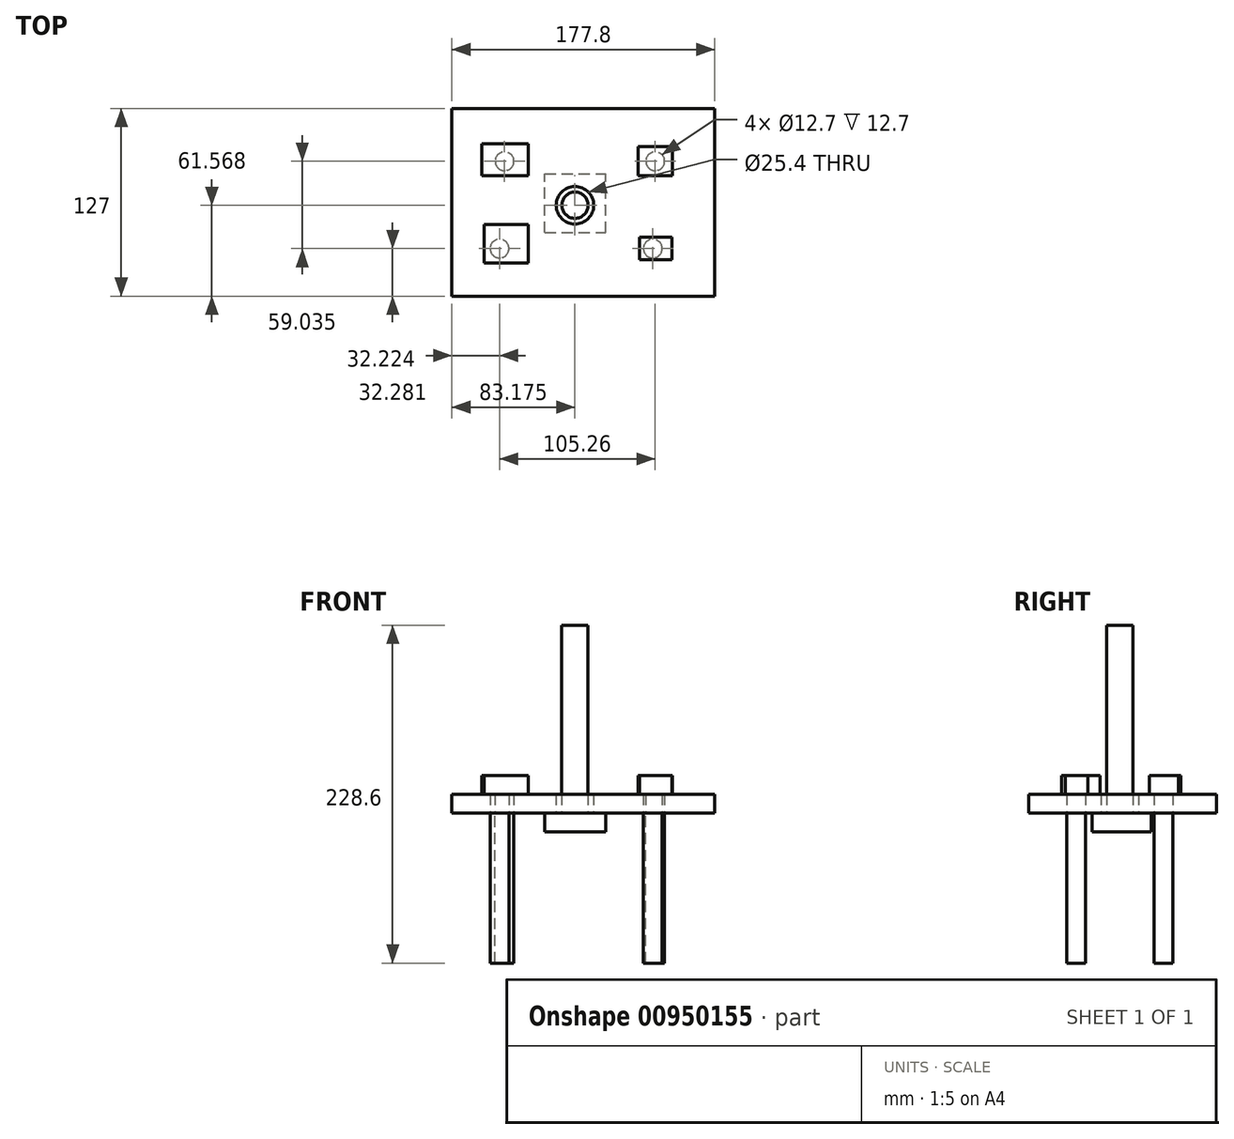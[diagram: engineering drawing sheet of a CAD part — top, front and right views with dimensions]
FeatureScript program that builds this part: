
annotation { "Feature Type Name" : "Feature", "Feature Type Description" : "" }
export const myFeature = defineFeature(function(context is Context, id is Id, definition is map)
    precondition{}
    {
        {
            var Q0;
            Q0=qCreatedBy(makeId("Top.planeOp"),FACE);
            var sketch = newSketch(context, id + "F0", { "sketchPlane" : qUnion([Q0])});
            skLineSegment(sketch, "E0.bottom", {"start": v(0, 0) * mm, "end": v(177.8, 0) * mm});
            skLineSegment(sketch, "E0.top", {"start": v(0, -127) * mm, "end": v(177.8, -127) * mm});
            skLineSegment(sketch, "E0.left", {"start": v(0, 0) * mm, "end": v(0, -127) * mm});
            skLineSegment(sketch, "E0.right", {"start": v(177.8, 0) * mm, "end": v(177.8, -127) * mm});
            skSolve(sketch);
        }
        {
            var Q0;
            Q0 = qSketchRegion(id + "F0", true);
            extrude(context, id + "F1", {"entities" : qUnion([Q0]), "depth" : 12.7 * mm, "offsetDistance" : 25.4 * mm});
        }
        {
            var Q0;
            Q0=makeQuery(id+"F1.opExtrude","CAP_FACE",FACE,{"disambiguationData":[OSD([sQuery(id+"F0.wireOp",EDGE,"E0.bottom"),sQuery(id+"F0.wireOp",EDGE,"E0.top"),sQuery(id+"F0.wireOp",EDGE,"E0.left"),sQuery(id+"F0.wireOp",EDGE,"E0.right")])],"isStart":true});
            var sketch = newSketch(context, id + "F2", { "sketchPlane" : qUnion([Q0])});
            skCircle(sketch, "E1", {"center": v(83.17, 65.43) * mm, "radius": 12.7 * mm});
            skCircle(sketch, "E2", {"center": v(135.81, 94.72) * mm, "radius": 6.35 * mm});
            skCircle(sketch, "E3", {"center": v(137.48, 35.68) * mm, "radius": 6.35 * mm});
            skCircle(sketch, "E4", {"center": v(35.57, 35.68) * mm, "radius": 6.35 * mm});
            skCircle(sketch, "E5", {"center": v(32.22, 94.72) * mm, "radius": 6.35 * mm});
            skSolve(sketch);
        }
        {
            var Q0;
            Q0 = qSketchRegion(id + "F2", true);
            extrude(context, id + "F3", {"entities" : qUnion([Q0]), "operationType" : NewBodyOperationType.REMOVE, "oppositeDirection" : true, "depth" : 25.4 * mm, "offsetDistance" : 25.4 * mm});
        }
        {
            var Q0;
            Q0=makeQuery(id+"F1.opExtrude","CAP_FACE",FACE,{"disambiguationData":[OSD([sQuery(id+"F0.wireOp",EDGE,"E0.bottom"),sQuery(id+"F0.wireOp",EDGE,"E0.top"),sQuery(id+"F0.wireOp",EDGE,"E0.left"),sQuery(id+"F0.wireOp",EDGE,"E0.right")])],"isStart":true});
            var sketch = newSketch(context, id + "F4", { "sketchPlane" : qUnion([Q0])});
            skCircle(sketch, "E6", {"center": v(83.17, 65.43) * mm, "radius": 8.9 * mm});
            skSolve(sketch);
        }
        {
            var Q0;
            Q0 = qSketchRegion(id + "F4", true);
            extrude(context, id + "F5", {"entities" : qUnion([Q0]), "oppositeDirection" : true, "depth" : 127 * mm, "offsetDistance" : 25.4 * mm});
        }
        {
            var Q0;
            Q0=makeQuery(id+"F1.opExtrude","CAP_FACE",FACE,{"disambiguationData":[OSD([sQuery(id+"F0.wireOp",EDGE,"E0.bottom"),sQuery(id+"F0.wireOp",EDGE,"E0.top"),sQuery(id+"F0.wireOp",EDGE,"E0.left"),sQuery(id+"F0.wireOp",EDGE,"E0.right")])],"isStart":true});
            var sketch = newSketch(context, id + "F6", { "sketchPlane" : qUnion([Q0])});
            skLineSegment(sketch, "E7.bottom", {"start": v(62.7, 84.02) * mm, "end": v(103.94, 84.02) * mm});
            skLineSegment(sketch, "E7.top", {"start": v(62.7, 44.15) * mm, "end": v(103.94, 44.15) * mm});
            skLineSegment(sketch, "E7.left", {"start": v(62.7, 84.02) * mm, "end": v(62.7, 44.15) * mm});
            skLineSegment(sketch, "E7.right", {"start": v(103.94, 84.02) * mm, "end": v(103.94, 44.15) * mm});
            skSolve(sketch);
        }
        {
            var Q0;
            Q0 = qSketchRegion(id + "F6", true);
            extrude(context, id + "F7", {"entities" : qUnion([Q0]), "depth" : 12.7 * mm, "offsetDistance" : 25.4 * mm});
        }
        {
            var Q0;
            Q0=makeQuery(id+"F1.opExtrude","CAP_FACE",FACE,{"disambiguationData":[OSD([sQuery(id+"F0.wireOp",EDGE,"E0.bottom"),sQuery(id+"F0.wireOp",EDGE,"E0.top"),sQuery(id+"F0.wireOp",EDGE,"E0.left"),sQuery(id+"F0.wireOp",EDGE,"E0.right")])],"isStart":false});
            var sketch = newSketch(context, id + "F8", { "sketchPlane" : qUnion([Q0])});
            skSolve(sketch);
        }
        {
            var Q0;
            Q0=makeQuery(id+"F1.opExtrude","CAP_FACE",FACE,{"disambiguationData":[OSD([sQuery(id+"F0.wireOp",EDGE,"E0.bottom"),sQuery(id+"F0.wireOp",EDGE,"E0.top"),sQuery(id+"F0.wireOp",EDGE,"E0.left"),sQuery(id+"F0.wireOp",EDGE,"E0.right")])],"isStart":true});
            var sketch = newSketch(context, id + "F9", { "sketchPlane" : qUnion([Q0])});
            skCircle(sketch, "E8", {"center": v(32.22, 94.72) * mm, "radius": 6.35 * mm});
            skCircle(sketch, "E9", {"center": v(135.81, 94.72) * mm, "radius": 6.35 * mm});
            skCircle(sketch, "E10", {"center": v(137.48, 35.68) * mm, "radius": 6.35 * mm});
            skCircle(sketch, "E11", {"center": v(35.57, 35.68) * mm, "radius": 6.35 * mm});
            skSolve(sketch);
        }
        {
            var Q0;
            Q0 = qSketchRegion(id + "F9", true);
            extrude(context, id + "F10", {"entities" : qUnion([Q0]), "depth" : 101.6 * mm, "offsetDistance" : 25.4 * mm});
        }
        {
            var Q0;
            {var subQ3=sQuery(id+"F0.wireOp",EDGE,"E0.bottom");Q0=makeQuery(id+"F8.imprint","IMPRINT",FACE,{"disambiguationData":[TD([[makeQuery(id+"F8.imprint","IMPRINT",EDGE,{"derivedFrom":makeQuery(id+"F1.opExtrude","CAP_EDGE",EDGE,{"disambiguationData":[OSD([subQ3])],"isStart":false})}),-1.0]])]});}
            var sketch = newSketch(context, id + "F11", { "sketchPlane" : qUnion([Q0])});
            skLineSegment(sketch, "E12.bottom", {"start": v(126.05, -25.77) * mm, "end": v(149.2, -25.77) * mm});
            skLineSegment(sketch, "E12.top", {"start": v(126.05, -45.4) * mm, "end": v(149.2, -45.4) * mm});
            skLineSegment(sketch, "E12.left", {"start": v(126.05, -25.77) * mm, "end": v(126.05, -45.4) * mm});
            skLineSegment(sketch, "E12.right", {"start": v(149.2, -25.77) * mm, "end": v(149.2, -45.4) * mm});
            skLineSegment(sketch, "E13.bottom", {"start": v(20.25, -24) * mm, "end": v(51.6, -24) * mm});
            skLineSegment(sketch, "E13.top", {"start": v(20.25, -45.4) * mm, "end": v(51.6, -45.4) * mm});
            skLineSegment(sketch, "E13.left", {"start": v(20.25, -24) * mm, "end": v(20.25, -45.4) * mm});
            skLineSegment(sketch, "E13.right", {"start": v(51.6, -24) * mm, "end": v(51.6, -45.4) * mm});
            skLineSegment(sketch, "E14.bottom", {"start": v(21.71, -78.52) * mm, "end": v(51.6, -78.52) * mm});
            skLineSegment(sketch, "E14.top", {"start": v(21.71, -104.6) * mm, "end": v(51.6, -104.6) * mm});
            skLineSegment(sketch, "E14.left", {"start": v(21.71, -78.52) * mm, "end": v(21.71, -104.6) * mm});
            skLineSegment(sketch, "E14.right", {"start": v(51.6, -78.52) * mm, "end": v(51.6, -104.6) * mm});
            skLineSegment(sketch, "E15.bottom", {"start": v(126.93, -87.02) * mm, "end": v(148.9, -87.02) * mm});
            skLineSegment(sketch, "E15.top", {"start": v(126.93, -102.26) * mm, "end": v(148.9, -102.26) * mm});
            skLineSegment(sketch, "E15.left", {"start": v(126.93, -87.02) * mm, "end": v(126.93, -102.26) * mm});
            skLineSegment(sketch, "E15.right", {"start": v(148.9, -87.02) * mm, "end": v(148.9, -102.26) * mm});
            skSolve(sketch);
        }
        {
            var Q0;
            Q0 = qSketchRegion(id + "F11", true);
            extrude(context, id + "F12", {"entities" : qUnion([Q0]), "operationType" : NewBodyOperationType.ADD, "depth" : 12.7 * mm, "offsetDistance" : 25.4 * mm});
        }
    });
